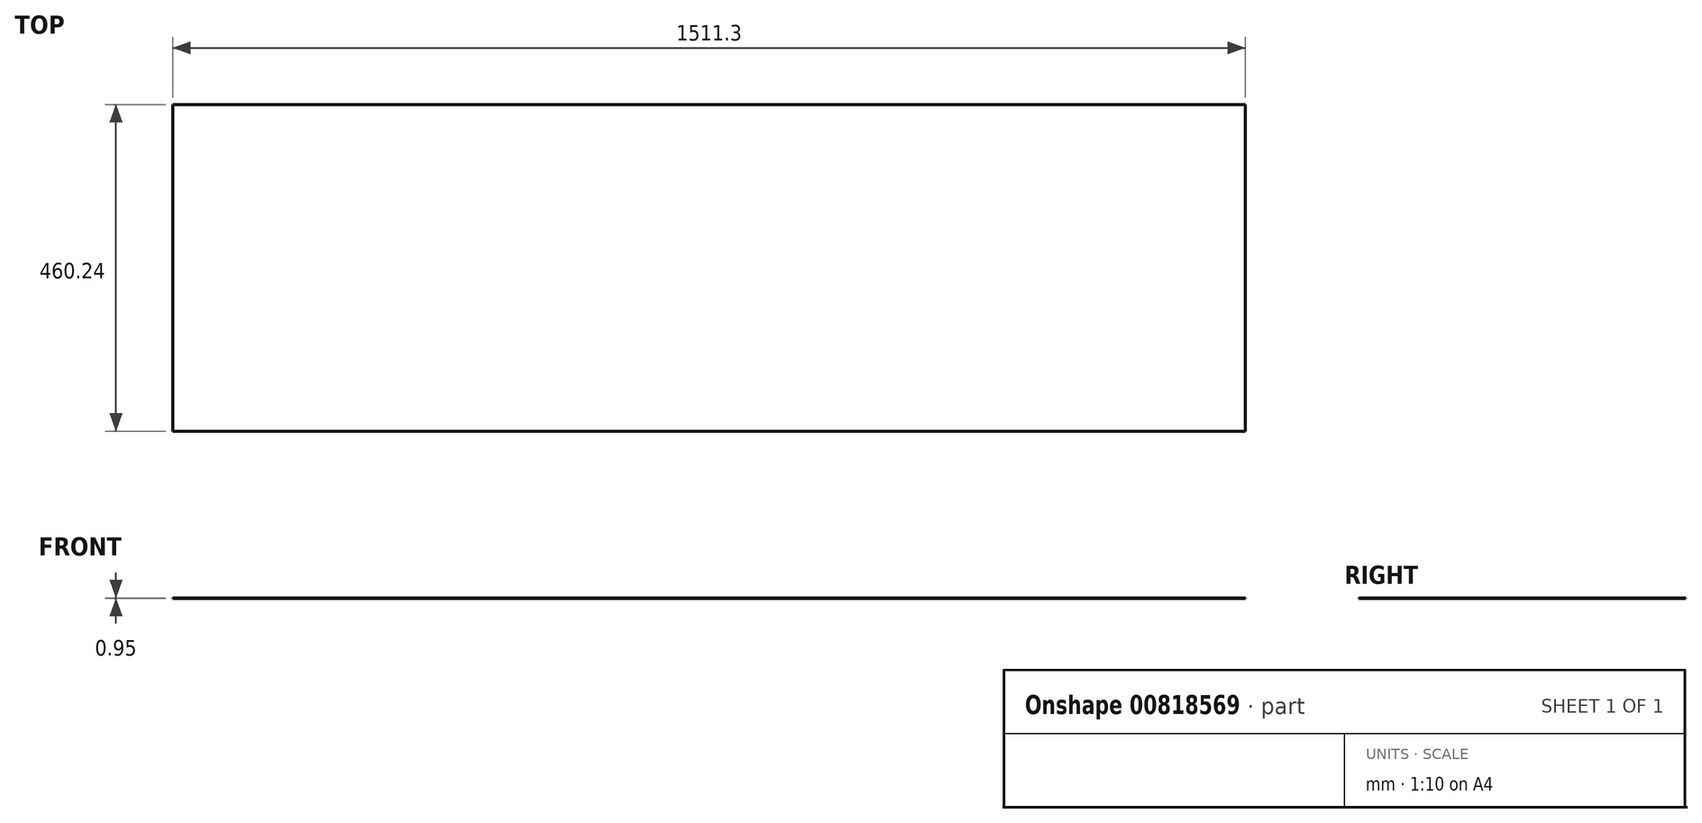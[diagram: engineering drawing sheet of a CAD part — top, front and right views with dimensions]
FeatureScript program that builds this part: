
annotation { "Feature Type Name" : "Feature", "Feature Type Description" : "" }
export const myFeature = defineFeature(function(context is Context, id is Id, definition is map)
    precondition{}
    {
        {
            var Q0;
            Q0=qCreatedBy(makeId("Top.planeOp"),FACE);
            var sketch = newSketch(context, id + "F0", { "sketchPlane" : qUnion([Q0])});
            skLineSegment(sketch, "E0.bottom", {"start": v(-756.07, 177.3) * mm, "end": v(755.23, 177.3) * mm});
            skLineSegment(sketch, "E0.top", {"start": v(-756.07, -282.95) * mm, "end": v(755.23, -282.95) * mm});
            skLineSegment(sketch, "E0.left", {"start": v(-756.07, 177.3) * mm, "end": v(-756.07, -282.95) * mm});
            skLineSegment(sketch, "E0.right", {"start": v(755.23, 177.3) * mm, "end": v(755.23, -282.95) * mm});
            skSolve(sketch);
        }
        {
            var Q0;
            Q0=makeQuery(id+"F0.imprint","IMPRINT",FACE,{"disambiguationData":[TD([[makeQuery(id+"F0.imprint","IMPRINT",EDGE,{"derivedFrom":sQuery(id+"F0.wireOp",EDGE,"E0.bottom")}),-1.0]])]});
            extrude(context, id + "F1", {"entities" : qUnion([Q0]), "depth" : 0.95 * mm, "offsetDistance" : 25.4 * mm});
        }
    });
